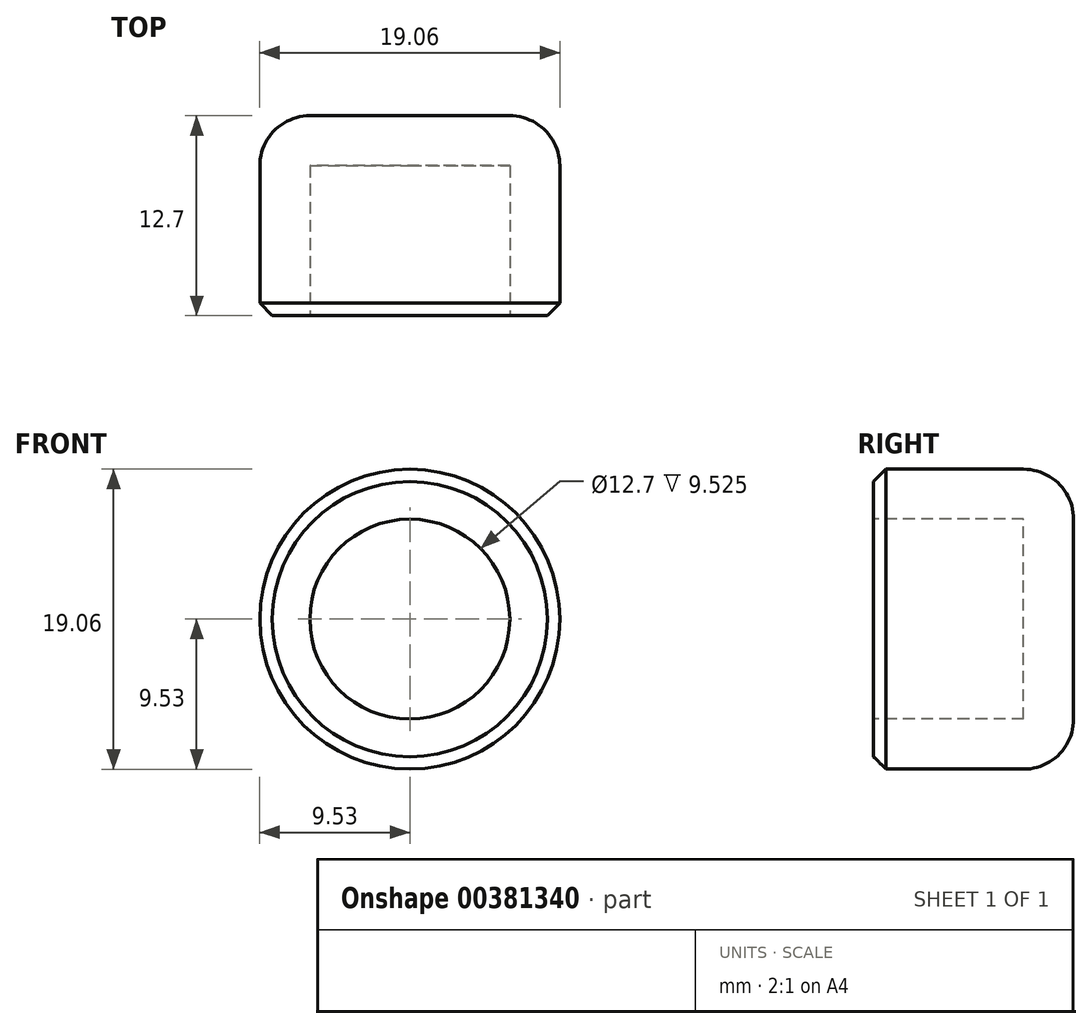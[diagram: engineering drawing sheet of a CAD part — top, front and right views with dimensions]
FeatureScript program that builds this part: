
annotation { "Feature Type Name" : "Feature", "Feature Type Description" : "" }
export const myFeature = defineFeature(function(context is Context, id is Id, definition is map)
    precondition{}
    {
        {
            var Q0;
            Q0=qCreatedBy(makeId("Front.planeOp"),FACE);
            var sketch = newSketch(context, id + "F0", { "sketchPlane" : qUnion([Q0])});
            skCircle(sketch, "E0", {"center": v(0, 0) * mm, "radius": 9.53 * mm});
            skSolve(sketch);
        }
        {
            var Q0;
            Q0=qSketchRegion(id+"F0",true);
            extrude(context, id + "F1", {"entities" : qUnion([Q0]), "depth" : 12.7 * mm});
        }
        {
            var Q0;
            Q0=makeQuery(id+"F1.opExtrude","CAP_FACE",FACE,{"disambiguationData":[OSD([sQuery(id+"F0.wireOp",EDGE,"E0")])],"isStart":false});
            var sketch = newSketch(context, id + "F2", { "sketchPlane" : qUnion([Q0])});
            skCircle(sketch, "E1", {"center": v(0, 0) * mm, "radius": 6.35 * mm});
            skSolve(sketch);
        }
        {
            var Q0;
            Q0=makeQuery(id+"F2.imprint","IMPRINT",FACE,{"disambiguationData":[TD([[makeQuery(id+"F2.imprint","IMPRINT",EDGE,{"derivedFrom":sQuery(id+"F2.wireOp",EDGE,"E1")}),1.0]])]});
            extrude(context, id + "F3", {"entities" : qUnion([Q0]), "operationType" : NewBodyOperationType.REMOVE, "oppositeDirection" : true, "depth" : 9.52 * mm});
        }
        {
            var Q0;
            Q0=makeQuery(id+"F1.opExtrude","CAP_EDGE",EDGE,{"disambiguationData":[OSD([sQuery(id+"F0.wireOp",EDGE,"E0")])],"isStart":true});
            fillet(context, id + "F4", {"entities" : qUnion([Q0]), "radius" : 3.17 * mm, "tangentPropagation" : true, "allowEdgeOverflow" : false});
        }
        {
            var Q0;
            Q0=makeQuery(id+"F1.opExtrude","CAP_EDGE",EDGE,{"disambiguationData":[OSD([sQuery(id+"F0.wireOp",EDGE,"E0")])],"isStart":false});
            chamfer(context, id + "F5", {"entities" : qUnion([Q0]), "chamferType" : ChamferType.OFFSET_ANGLE, "width" : 0.79 * mm, "oppositeDirection" : false, "angle" : 45 * degree, "tangentPropagation" : true});
        }
    });
